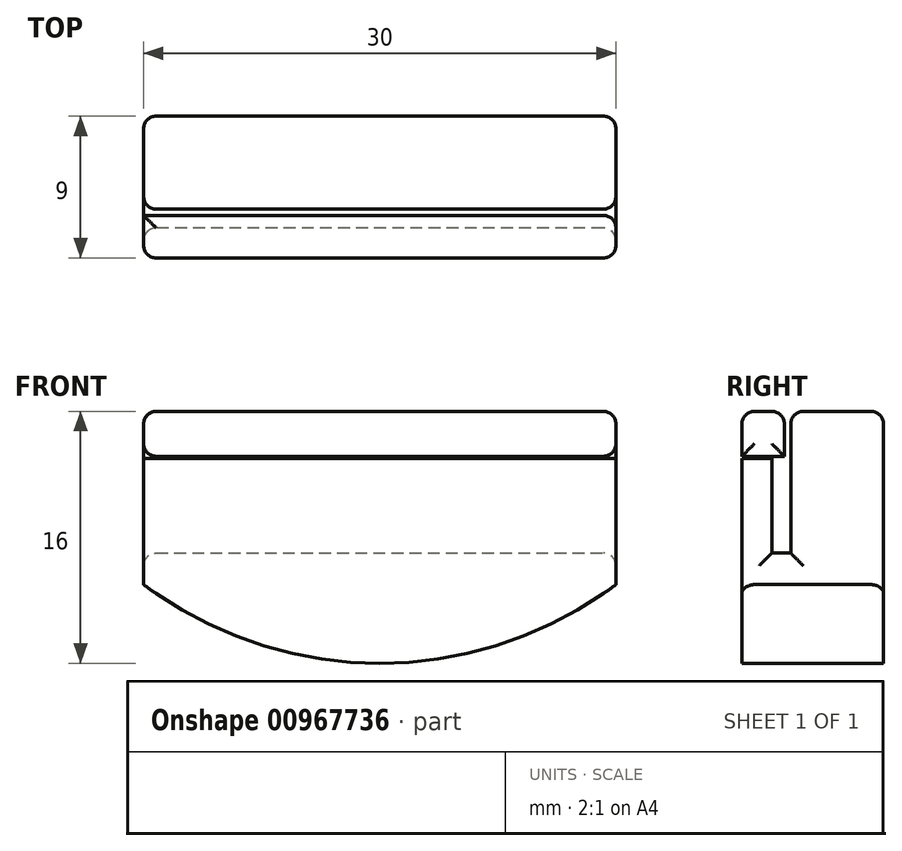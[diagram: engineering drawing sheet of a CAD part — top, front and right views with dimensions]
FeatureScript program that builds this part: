
annotation { "Feature Type Name" : "Feature", "Feature Type Description" : "" }
export const myFeature = defineFeature(function(context is Context, id is Id, definition is map)
    precondition{}
    {
        {
            var Q0;
            Q0=qCreatedBy(makeId("Top.planeOp"),FACE);
            var sketch = newSketch(context, id + "F0", { "sketchPlane" : qUnion([Q0])});
            skLineSegment(sketch, "E0.bottom", {"start": v(15, 4.5) * mm, "end": v(-15, 4.5) * mm});
            skLineSegment(sketch, "E0.top", {"start": v(15, -4.5) * mm, "end": v(-15, -4.5) * mm});
            skLineSegment(sketch, "E0.left", {"start": v(15, 4.5) * mm, "end": v(15, -4.5) * mm});
            skLineSegment(sketch, "E0.right", {"start": v(-15, 4.5) * mm, "end": v(-15, -4.5) * mm});
            skPoint(sketch, "E0.middle", {"position": v(0, 0) * mm});
            skLineSegment(sketch, "E1", {"start": v(-15, -1.4) * mm, "end": v(15, -1.4) * mm});
            skLineSegment(sketch, "E2", {"start": v(15, -2.6) * mm, "end": v(-15, -2.6) * mm});
            skSolve(sketch);
        }
        {
            var Q0;
            {var subQ0=sQuery(id+"F0.wireOp",EDGE,"E0.bottom");Q0=makeQuery(id+"F0.imprint","IMPRINT",FACE,{"disambiguationData":[TD([[makeQuery(id+"F0.imprint","IMPRINT",EDGE,{"derivedFrom":subQ0}),1.0]])]});}
            extrude(context, id + "F1", {"entities" : qUnion([Q0]), "depth" : 16 * mm, "offsetDistance" : 25 * mm});
        }
        {
            var Q0;
            {var subQ0=sQuery(id+"F0.wireOp",EDGE,"E0.top");Q0=makeQuery(id+"F0.imprint","IMPRINT",FACE,{"disambiguationData":[TD([[makeQuery(id+"F0.imprint","IMPRINT",EDGE,{"derivedFrom":subQ0}),-1.0]])]});}
            extrude(context, id + "F2", {"entities" : qUnion([Q0]), "depth" : 13 * mm, "offsetDistance" : 25 * mm});
        }
        {
            var Q0;
            {var subQ0=sQuery(id+"F0.wireOp",EDGE,"E1");Q0=makeQuery(id+"F0.imprint","IMPRINT",FACE,{"disambiguationData":[TD([[makeQuery(id+"F0.imprint","IMPRINT",EDGE,{"derivedFrom":subQ0}),-1.0]])]});}
            extrude(context, id + "F3", {"entities" : qUnion([Q0]), "operationType" : NewBodyOperationType.ADD, "depth" : 7 * mm, "offsetDistance" : 25 * mm});
        }
        {
            var Q0;
            Q0=makeQuery(id+"F2.opExtrude","SWEPT_FACE",FACE,{"disambiguationData":[OSD([sQuery(id+"F0.wireOp",EDGE,"E0.top")])]});
            var sketch = newSketch(context, id + "F4", { "sketchPlane" : qUnion([Q0])});
            skLineSegment(sketch, "E3", {"start": v(-15, 5) * mm, "end": v(15, 5) * mm, "construction": true});
            skArc(sketch, "E4", {"start": v(-15, 5) * mm, "mid": v(0, 0) * mm, "end": v(15, 5) * mm});
            skSolve(sketch);
        }
        {
            var Q0;
            {var subQ0=sQuery(id+"F4.wireOp",EDGE,"E4");var subQ1=sQuery(id+"F0.wireOp",EDGE,"E0.top");var subQ4=makeQuery(id+"F2.opExtrude","CAP_EDGE",EDGE,{"disambiguationData":[OSD([subQ1])],"isStart":true});var subQ5=makeQuery(id+"F4.imprint","INTERSECT",VERTEX,{"derivedFrom":[subQ4,subQ0]});Q0=makeQuery(id+"F4.imprint","IMPRINT",FACE,{"disambiguationData":[TD([[makeQuery(id+"F4.imprint","IMPRINT",EDGE,{"disambiguationData":[TD([[subQ5,1.0]])],"derivedFrom":subQ0}),-1.0]])]});}
            var Q1;
            {var subQ0=sQuery(id+"F4.wireOp",EDGE,"E4");var subQ1=sQuery(id+"F0.wireOp",EDGE,"E0.top");var subQ4=makeQuery(id+"F2.opExtrude","CAP_EDGE",EDGE,{"disambiguationData":[OSD([subQ1])],"isStart":true});var subQ5=makeQuery(id+"F4.imprint","INTERSECT",VERTEX,{"derivedFrom":[subQ4,subQ0]});Q1=makeQuery(id+"F4.imprint","IMPRINT",FACE,{"disambiguationData":[TD([[makeQuery(id+"F4.imprint","IMPRINT",EDGE,{"disambiguationData":[TD([[subQ5,-1.0]])],"derivedFrom":subQ0}),-1.0]])]});}
            extrude(context, id + "F5", {"entities" : qUnion([Q0, Q1]), "operationType" : NewBodyOperationType.REMOVE, "endBound" : BoundingType.THROUGH_ALL, "oppositeDirection" : true, "depth" : 25 * mm, "offsetDistance" : 25 * mm});
        }
        {
            var Q0;
            Q0=makeQuery(id+"F1.opExtrude","CAP_FACE",FACE,{"disambiguationData":[OSD([sQuery(id+"F0.wireOp",EDGE,"E0.bottom"),sQuery(id+"F0.wireOp",EDGE,"E0.left"),sQuery(id+"F0.wireOp",EDGE,"E0.right"),sQuery(id+"F0.wireOp",EDGE,"E1")])],"isStart":false});
            var sketch = newSketch(context, id + "F6", { "sketchPlane" : qUnion([Q0])});
            skLineSegment(sketch, "E5.0.0", {"start": v(-15, -4.5) * mm, "end": v(15, -4.5) * mm});
            skLineSegment(sketch, "E5.0.1", {"start": v(15, -4.5) * mm, "end": v(15, -2.6) * mm});
            skLineSegment(sketch, "E5.0.2", {"start": v(15, -2.6) * mm, "end": v(-15, -2.6) * mm});
            skLineSegment(sketch, "E5.0.3", {"start": v(-15, -2.6) * mm, "end": v(-15, -4.5) * mm});
            skSolve(sketch);
        }
        {
            var Q0;
            Q0=makeQuery(id+"F6.imprint","IMPRINT",FACE,{"disambiguationData":[TD([[makeQuery(id+"F6.imprint","IMPRINT",EDGE,{"derivedFrom":sQuery(id+"F6.wireOp",EDGE,"E5.0.0")}),1.0]])]});
            extrude(context, id + "F7", {"entities" : qUnion([Q0]), "endBound" : BoundingType.UP_TO_NEXT, "oppositeDirection" : true, "depth" : 25 * mm, "hasOffset" : true, "offsetDistance" : .15 * mm, "hasSecondDirectionOffset" : true, "secondDirectionOffsetDistance" : 25 * mm});
        }
        {
            var Q0;
            Q0=makeQuery(id+"F7.opExtrude","SWEPT_FACE",FACE,{"disambiguationData":[OSD([sQuery(id+"F6.wireOp",EDGE,"E5.0.2")])]});
            extrude(context, id + "F8", {"entities" : qUnion([Q0]), "operationType" : NewBodyOperationType.ADD, "endBound" : BoundingType.UP_TO_NEXT, "depth" : 25 * mm, "hasOffset" : true, "offsetDistance" : .4 * mm});
        }
        {
            var Q0;
            Q0=makeQuery(id+"F5.boolean.opBoolean","COPY",EDGE,{"derivedFrom":makeQuery(id+"F5.opExtrude","SWEPT_EDGE",EDGE,{"disambiguationData":[OSD([sQuery(id+"F0.wireOp",EDGE,"E0.top"),sQuery(id+"F0.wireOp",EDGE,"E0.right"),sQuery(id+"F4.wireOp",EDGE,"E4")])]})});
            var Q1;
            {var subQ0=sQuery(id+"F4.wireOp",EDGE,"E4");var subQ1=sQuery(id+"F0.wireOp",EDGE,"E0.top");var subQ2=makeQuery(id+"F4.imprint","INTERSECT",VERTEX,{"derivedFrom":[makeQuery(id+"F2.opExtrude","CAP_EDGE",EDGE,{"disambiguationData":[OSD([subQ1])],"isStart":true}),subQ0]});Q1=makeQuery(id+"F5.boolean.opBoolean","MERGE",EDGE,{"derivedFrom":[],"fromTools":[makeQuery(id+"F5.opExtrude","CAP_EDGE",EDGE,{"disambiguationData":[OSD([subQ0]),TDD([makeQuery(id+"F4.imprint","IMPRINT",EDGE,{"disambiguationData":[TD([[subQ2,1.0]])],"derivedFrom":subQ0})])],"isStart":true}),makeQuery(id+"F5.opExtrude","CAP_EDGE",EDGE,{"disambiguationData":[OSD([subQ0]),TDD([makeQuery(id+"F4.imprint","IMPRINT",EDGE,{"disambiguationData":[TD([[subQ2,-1.0]])],"derivedFrom":subQ0})])],"isStart":true})]});}
            var Q2;
            Q2=makeQuery(id+"F5.boolean.opBoolean","COPY",EDGE,{"derivedFrom":makeQuery(id+"F5.opExtrude","SWEPT_EDGE",EDGE,{"disambiguationData":[OSD([sQuery(id+"F0.wireOp",EDGE,"E0.top"),sQuery(id+"F0.wireOp",EDGE,"E0.left"),sQuery(id+"F4.wireOp",EDGE,"E4")])]})});
            var Q3;
            {var subQ0=sQuery(id+"F4.wireOp",EDGE,"E4");var subQ1=sQuery(id+"F0.wireOp",EDGE,"E0.top");var subQ2=makeQuery(id+"F4.imprint","INTERSECT",VERTEX,{"derivedFrom":[makeQuery(id+"F2.opExtrude","CAP_EDGE",EDGE,{"disambiguationData":[OSD([subQ1])],"isStart":true}),subQ0]});Q3=makeQuery(id+"F5.boolean.opBoolean","MERGE",EDGE,{"derivedFrom":[],"fromTools":[makeQuery(id+"F5.opExtrude","CAP_EDGE",EDGE,{"disambiguationData":[OSD([subQ0]),TDD([makeQuery(id+"F4.imprint","IMPRINT",EDGE,{"disambiguationData":[TD([[subQ2,1.0]])],"derivedFrom":subQ0})])],"isStart":true}),makeQuery(id+"F5.opExtrude","CAP_EDGE",EDGE,{"disambiguationData":[OSD([subQ0]),TDD([makeQuery(id+"F4.imprint","IMPRINT",EDGE,{"disambiguationData":[TD([[subQ2,-1.0]])],"derivedFrom":subQ0})])],"isStart":true})]});}
            var Q4;
            Q4=makeQuery(id+"F2.opExtrude","SWEPT_EDGE",EDGE,{"disambiguationData":[OSD([sQuery(id+"F0.wireOp",EDGE,"E0.top"),sQuery(id+"F0.wireOp",EDGE,"E0.right")])]});
            var Q5;
            Q5=makeQuery(id+"F2.opExtrude","SWEPT_EDGE",EDGE,{"disambiguationData":[OSD([sQuery(id+"F0.wireOp",EDGE,"E0.right"),sQuery(id+"F0.wireOp",EDGE,"E2")])]});
            var Q6;
            Q6=makeQuery(id+"F1.opExtrude","SWEPT_EDGE",EDGE,{"disambiguationData":[OSD([sQuery(id+"F0.wireOp",EDGE,"E0.right"),sQuery(id+"F0.wireOp",EDGE,"E1")])]});
            var Q7;
            Q7=makeQuery(id+"F3.opExtrude","CAP_EDGE",EDGE,{"disambiguationData":[OSD([sQuery(id+"F0.wireOp",EDGE,"E0.right")])],"isStart":false});
            var Q8;
            Q8=makeQuery(id+"F1.opExtrude","CAP_EDGE",EDGE,{"disambiguationData":[OSD([sQuery(id+"F0.wireOp",EDGE,"E0.right")])],"isStart":false});
            var Q9;
            Q9=makeQuery(id+"F8.opExtrude","TWEAK_EDGE",EDGE,{"derivedFrom":[makeQuery(id+"F1.opExtrude","SWEPT_FACE",FACE,{"disambiguationData":[OSD([sQuery(id+"F0.wireOp",EDGE,"E1")])]}),makeQuery(id+"F7.opExtrude","SWEPT_EDGE",EDGE,{"disambiguationData":[OSD([sQuery(id+"F6.wireOp",EDGE,"E5.0.2"),sQuery(id+"F6.wireOp",EDGE,"E5.0.3")])]})]});
            var Q10;
            Q10=makeQuery(id+"F7.opExtrude","SWEPT_EDGE",EDGE,{"disambiguationData":[OSD([sQuery(id+"F6.wireOp",EDGE,"E5.0.0"),sQuery(id+"F6.wireOp",EDGE,"E5.0.3")])]});
            var Q11;
            Q11=makeQuery(id+"F8.boolean.opBoolean","MERGE",EDGE,{"derivedFrom":[makeQuery(id+"F7.opExtrude","CAP_EDGE",EDGE,{"disambiguationData":[OSD([sQuery(id+"F6.wireOp",EDGE,"E5.0.3")])],"isStart":true}),makeQuery(id+"F8.opExtrude","SWEPT_EDGE",EDGE,{"disambiguationData":[OSD([sQuery(id+"F0.wireOp",EDGE,"E0.right"),sQuery(id+"F0.wireOp",EDGE,"E1")])]})]});
            var Q12;
            Q12=makeQuery(id+"F7.opExtrude","CAP_EDGE",EDGE,{"disambiguationData":[OSD([sQuery(id+"F6.wireOp",EDGE,"E5.0.0")])],"isStart":true});
            var Q13;
            Q13=makeQuery(id+"F7.opExtrude","SWEPT_EDGE",EDGE,{"disambiguationData":[OSD([sQuery(id+"F6.wireOp",EDGE,"E5.0.0"),sQuery(id+"F6.wireOp",EDGE,"E5.0.1")])]});
            var Q14;
            Q14=makeQuery(id+"F8.opExtrude","CAP_EDGE",EDGE,{"disambiguationData":[OSD([sQuery(id+"F0.wireOp",EDGE,"E0.left"),sQuery(id+"F0.wireOp",EDGE,"E1")])],"isStart":false});
            var Q15;
            Q15=makeQuery(id+"F8.boolean.opBoolean","MERGE",EDGE,{"derivedFrom":[makeQuery(id+"F7.opExtrude","CAP_EDGE",EDGE,{"disambiguationData":[OSD([sQuery(id+"F6.wireOp",EDGE,"E5.0.1")])],"isStart":true}),makeQuery(id+"F8.opExtrude","SWEPT_EDGE",EDGE,{"disambiguationData":[OSD([sQuery(id+"F0.wireOp",EDGE,"E0.left"),sQuery(id+"F0.wireOp",EDGE,"E1")])]})]});
            var Q16;
            Q16=makeQuery(id+"F1.opExtrude","SWEPT_EDGE",EDGE,{"disambiguationData":[OSD([sQuery(id+"F0.wireOp",EDGE,"E0.left"),sQuery(id+"F0.wireOp",EDGE,"E1")])]});
            var Q17;
            Q17=makeQuery(id+"F2.opExtrude","SWEPT_EDGE",EDGE,{"disambiguationData":[OSD([sQuery(id+"F0.wireOp",EDGE,"E0.left"),sQuery(id+"F0.wireOp",EDGE,"E2")])]});
            var Q18;
            Q18=makeQuery(id+"F2.opExtrude","SWEPT_EDGE",EDGE,{"disambiguationData":[OSD([sQuery(id+"F0.wireOp",EDGE,"E0.top"),sQuery(id+"F0.wireOp",EDGE,"E0.left")])]});
            var Q19;
            Q19=makeQuery(id+"F3.opExtrude","CAP_EDGE",EDGE,{"disambiguationData":[OSD([sQuery(id+"F0.wireOp",EDGE,"E0.left")])],"isStart":false});
            var Q20;
            Q20=makeQuery(id+"F1.opExtrude","CAP_EDGE",EDGE,{"disambiguationData":[OSD([sQuery(id+"F0.wireOp",EDGE,"E0.left")])],"isStart":false});
            var Q21;
            Q21=makeQuery(id+"F1.opExtrude","CAP_EDGE",EDGE,{"disambiguationData":[OSD([sQuery(id+"F0.wireOp",EDGE,"E1")])],"isStart":false});
            var Q22;
            Q22=makeQuery(id+"F1.opExtrude","SWEPT_EDGE",EDGE,{"disambiguationData":[OSD([sQuery(id+"F0.wireOp",EDGE,"E0.bottom"),sQuery(id+"F0.wireOp",EDGE,"E0.right")])]});
            var Q23;
            Q23=makeQuery(id+"F1.opExtrude","SWEPT_EDGE",EDGE,{"disambiguationData":[OSD([sQuery(id+"F0.wireOp",EDGE,"E0.bottom"),sQuery(id+"F0.wireOp",EDGE,"E0.left")])]});
            var Q24;
            Q24=makeQuery(id+"F1.opExtrude","CAP_EDGE",EDGE,{"disambiguationData":[OSD([sQuery(id+"F0.wireOp",EDGE,"E0.bottom")])],"isStart":false});
            var Q25;
            Q25=makeQuery(id+"F8.opExtrude","CAP_EDGE",EDGE,{"disambiguationData":[OSD([sQuery(id+"F0.wireOp",EDGE,"E1")])],"isStart":false});
            fillet(context, id + "F9", {"entities" : qUnion([Q0, Q1, Q2, Q3, Q4, Q5, Q6, Q7, Q8, Q9, Q10, Q11, Q12, Q13, Q14, Q15, Q16, Q17, Q18, Q19, Q20, Q21, Q22, Q23, Q24, Q25]), "radius" : .8 * mm, "tangentPropagation" : true, "allowEdgeOverflow" : false});
        }
    });
